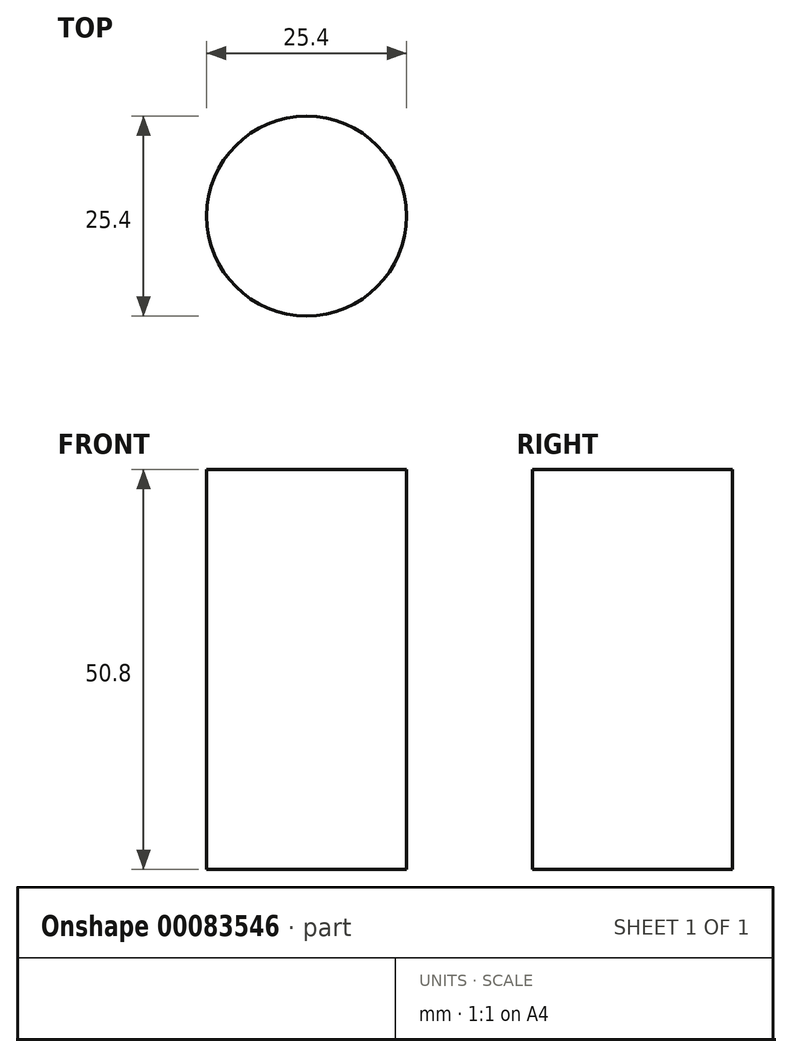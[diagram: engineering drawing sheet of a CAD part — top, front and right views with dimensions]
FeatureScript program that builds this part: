
annotation { "Feature Type Name" : "Feature", "Feature Type Description" : "" }
export const myFeature = defineFeature(function(context is Context, id is Id, definition is map)
    precondition{}
    {
        {
            var Q0;
            Q0=qCreatedBy(makeId("Top.planeOp"),FACE);
            var sketch = newSketch(context, id + "F0", { "sketchPlane" : qUnion([Q0])});
            skCircle(sketch, "E0", {"center": v(0, 0) * mm, "radius": 12.7 * mm});
            skSolve(sketch);
        }
        {
            var Q0;
            Q0 = qSketchRegion(id + "F0", true);
            extrude(context, id + "F1", {"entities" : qUnion([Q0]), "depth" : 50.8 * mm});
        }
    });
